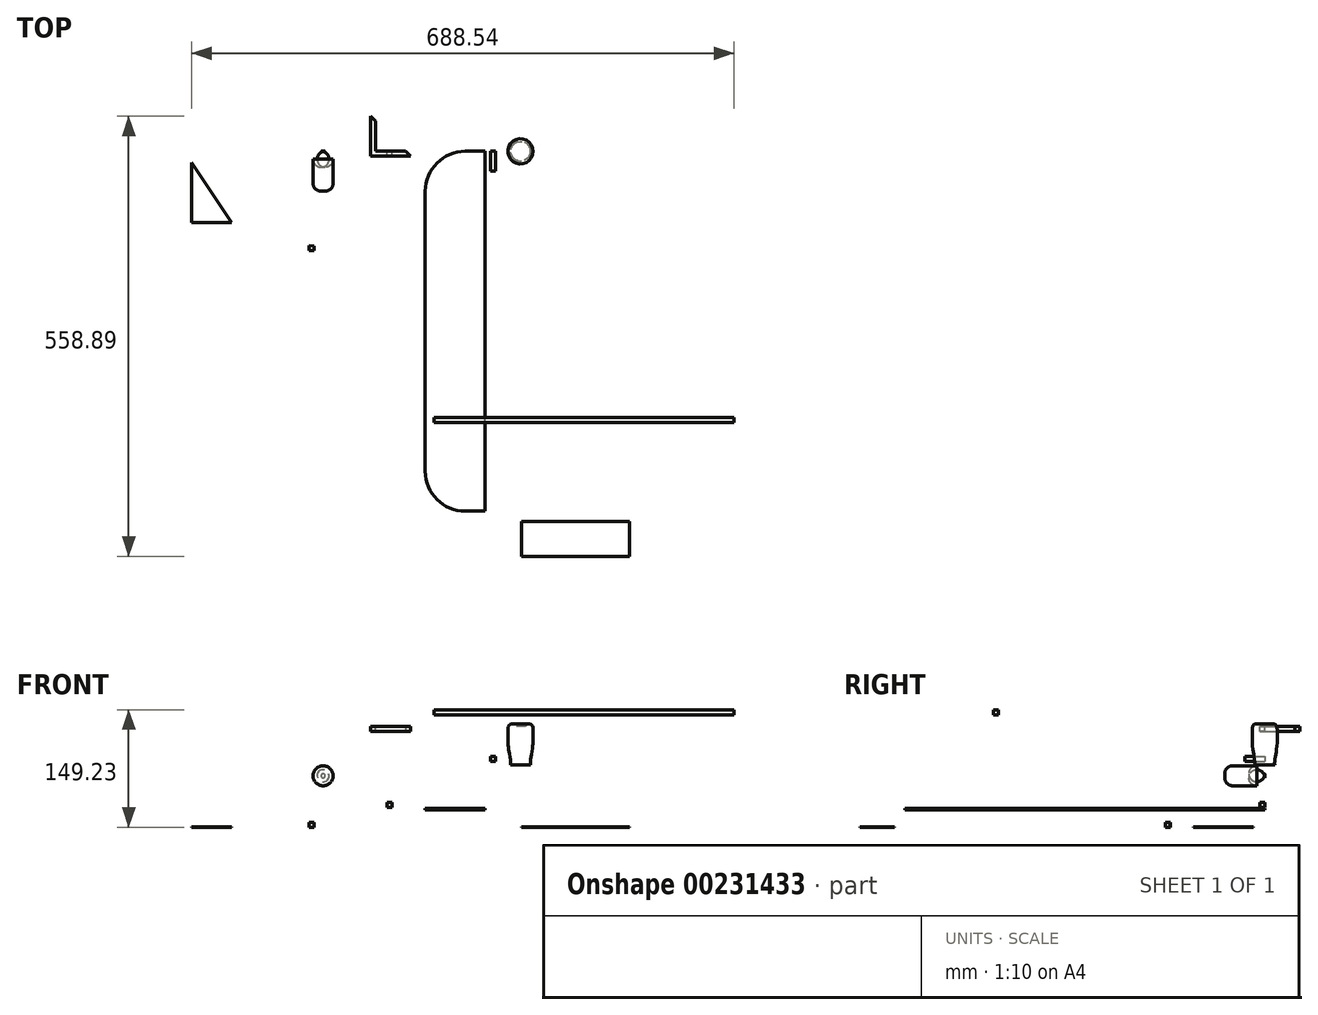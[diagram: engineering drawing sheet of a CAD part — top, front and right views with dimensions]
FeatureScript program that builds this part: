
annotation { "Feature Type Name" : "Feature", "Feature Type Description" : "" }
export const myFeature = defineFeature(function(context is Context, id is Id, definition is map)
    precondition{}
    {
        {
            var Q0;
            Q0=qCreatedBy(makeId("Front.planeOp"),FACE);
            var sketch = newSketch(context, id + "F0", { "sketchPlane" : qUnion([Q0])});
            skLineSegment(sketch, "E0.bottom", {"start": v(-10.86, 23.84) * mm, "end": v(65.34, 23.84) * mm});
            skLineSegment(sketch, "E0.top", {"start": v(-10.86, 22.25) * mm, "end": v(65.34, 22.25) * mm});
            skLineSegment(sketch, "E0.left", {"start": v(-10.86, 23.84) * mm, "end": v(-10.86, 22.25) * mm});
            skLineSegment(sketch, "E0.right", {"start": v(65.34, 23.84) * mm, "end": v(65.34, 22.25) * mm});
            skSolve(sketch);
        }
        {
            var Q0;
            Q0=makeQuery(id+"F0.imprint","IMPRINT",FACE,{"disambiguationData":[TD([[makeQuery(id+"F0.imprint","IMPRINT",EDGE,{"derivedFrom":sQuery(id+"F0.wireOp",EDGE,"E0.bottom")}),-1.0]])]});
            extrude(context, id + "F1", {"entities" : qUnion([Q0]), "depth" : 457.2 * mm});
        }
        {
            var Q0;
            Q0=qCreatedBy(makeId("Right.planeOp"),FACE);
            var sketch = newSketch(context, id + "F2", { "sketchPlane" : qUnion([Q0])});
            skLineSegment(sketch, "E1.bottom", {"start": v(-344.61, 149.23) * mm, "end": v(-338.26, 149.23) * mm});
            skLineSegment(sketch, "E1.top", {"start": v(-344.61, 142.88) * mm, "end": v(-338.26, 142.88) * mm});
            skLineSegment(sketch, "E1.left", {"start": v(-344.61, 149.23) * mm, "end": v(-344.61, 142.88) * mm});
            skLineSegment(sketch, "E1.right", {"start": v(-338.26, 149.23) * mm, "end": v(-338.26, 142.88) * mm});
            skSolve(sketch);
        }
        {
            var Q0;
            Q0=makeQuery(id+"F2.imprint","IMPRINT",FACE,{"disambiguationData":[TD([[makeQuery(id+"F2.imprint","IMPRINT",EDGE,{"derivedFrom":sQuery(id+"F2.wireOp",EDGE,"E1.bottom")}),-1.0]])]});
            extrude(context, id + "F3", {"entities" : qUnion([Q0]), "depth" : 381 * mm});
        }
        {
            var Q0;
            Q0=qCreatedBy(makeId("Front.planeOp"),FACE);
            var sketch = newSketch(context, id + "F4", { "sketchPlane" : qUnion([Q0])});
            skLineSegment(sketch, "E2.bottom", {"start": v(-80.6, 122) * mm, "end": v(-74.24, 122) * mm});
            skLineSegment(sketch, "E2.top", {"start": v(-80.6, 71.2) * mm, "end": v(-74.24, 71.2) * mm});
            skLineSegment(sketch, "E2.left", {"start": v(-80.6, 122) * mm, "end": v(-80.6, 71.2) * mm});
            skLineSegment(sketch, "E2.right", {"start": v(-74.24, 122) * mm, "end": v(-74.24, 71.2) * mm});
            skLineSegment(sketch, "E3.bottom", {"start": v(-74.24, 122) * mm, "end": v(-29.8, 122) * mm});
            skLineSegment(sketch, "E3.top", {"start": v(-74.24, 115.65) * mm, "end": v(-29.8, 115.65) * mm});
            skLineSegment(sketch, "E3.left", {"start": v(-74.24, 122) * mm, "end": v(-74.24, 115.65) * mm});
            skLineSegment(sketch, "E3.right", {"start": v(-29.8, 122) * mm, "end": v(-29.8, 115.65) * mm});
            skSolve(sketch);
        }
        {
            var Q0;
            Q0=makeQuery(id+"F4.imprint","IMPRINT",FACE,{"disambiguationData":[TD([[makeQuery(id+"F4.imprint","IMPRINT",EDGE,{"derivedFrom":sQuery(id+"F4.wireOp",EDGE,"E3.bottom")}),-1.0]])]});
            var Q1;
            Q1=makeQuery(id+"F4.imprint","IMPRINT",FACE,{"disambiguationData":[TD([[makeQuery(id+"F4.imprint","IMPRINT",EDGE,{"derivedFrom":sQuery(id+"F4.wireOp",EDGE,"E2.bottom")}),-1.0]])]});
            extrude(context, id + "F5", {"entities" : qUnion([Q0, Q1]), "depth" : 6.35 * mm});
        }
        {
            var Q0;
            Q0=makeQuery(id+"F5.opExtrude","SWEPT_EDGE",EDGE,{"disambiguationData":[OSD([sQuery(id+"F4.wireOp",EDGE,"E3.top"),sQuery(id+"F4.wireOp",EDGE,"E3.right")])]});
            chamfer(context, id + "F6", {"entities" : qUnion([Q0]), "chamferType" : ChamferType.OFFSET_ANGLE, "width" : 6.35 * mm, "oppositeDirection" : false, "angle" : 45 * degree, "tangentPropagation" : true});
        }
        {
            var Q0;
            Q0=makeQuery(id+"F5.opExtrude","SWEPT_EDGE",EDGE,{"disambiguationData":[OSD([sQuery(id+"F4.wireOp",EDGE,"E2.top"),sQuery(id+"F4.wireOp",EDGE,"E2.right")])]});
            chamfer(context, id + "F7", {"entities" : qUnion([Q0]), "chamferType" : ChamferType.OFFSET_ANGLE, "width" : 6.35 * mm, "oppositeDirection" : false, "angle" : 45 * degree, "tangentPropagation" : true});
        }
        {
            var Q0;
            Q0=makeQuery(id+"F5.opExtrude","SWEPT_BODY",BODY,{"disambiguationData":[OSD([sQuery(id+"F4.wireOp",EDGE,"E2.bottom"),sQuery(id+"F4.wireOp",EDGE,"E2.top"),sQuery(id+"F4.wireOp",EDGE,"E2.left"),sQuery(id+"F4.wireOp",EDGE,"E2.right"),sQuery(id+"F4.wireOp",EDGE,"E3.bottom"),sQuery(id+"F4.wireOp",EDGE,"E3.top"),sQuery(id+"F4.wireOp",EDGE,"E3.right")])]});
            var Q1;
            Q1=makeQuery(id+"F5.opExtrude","CAP_EDGE",EDGE,{"disambiguationData":[OSD([sQuery(id+"F4.wireOp",EDGE,"E2.bottom"),sQuery(id+"F4.wireOp",EDGE,"E3.bottom")])],"isStart":false});
            transform(context, id + "F8", {"entities" : qUnion([Q0]), "transformType" : TransformType.ROTATION, "transformAxis" : qUnion([Q1]), "angle" : 90 * degree, "makeCopy" : false});
        }
        {
            var Q0;
            Q0=qCreatedBy(makeId("Front.planeOp"),FACE);
            var sketch = newSketch(context, id + "F9", { "sketchPlane" : qUnion([Q0])});
            skLineSegment(sketch, "E4.bottom", {"start": v(-59.33, 31.83) * mm, "end": v(-52.98, 31.83) * mm});
            skLineSegment(sketch, "E4.top", {"start": v(-59.33, 25.48) * mm, "end": v(-52.98, 25.48) * mm});
            skLineSegment(sketch, "E4.left", {"start": v(-59.33, 31.83) * mm, "end": v(-59.33, 25.48) * mm});
            skLineSegment(sketch, "E4.right", {"start": v(-52.98, 31.83) * mm, "end": v(-52.98, 25.48) * mm});
            skSolve(sketch);
        }
        {
            var Q0;
            Q0=makeQuery(id+"F9.imprint","IMPRINT",FACE,{"disambiguationData":[TD([[makeQuery(id+"F9.imprint","IMPRINT",EDGE,{"derivedFrom":sQuery(id+"F9.wireOp",EDGE,"E4.bottom")}),-1.0]])]});
            extrude(context, id + "F10", {"entities" : qUnion([Q0]), "depth" : 6.35 * mm});
        }
        {
            var Q0;
            Q0=makeQuery(id+"F1.opExtrude","CAP_EDGE",EDGE,{"disambiguationData":[OSD([sQuery(id+"F0.wireOp",EDGE,"E0.left")])],"isStart":false});
            fillet(context, id + "F11", {"entities" : qUnion([Q0]), "radius" : 50.8 * mm, "tangentPropagation" : true, "allowEdgeOverflow" : false});
        }
        {
            var Q0;
            Q0=makeQuery(id+"F1.opExtrude","CAP_EDGE",EDGE,{"disambiguationData":[OSD([sQuery(id+"F0.wireOp",EDGE,"E0.left")])],"isStart":true});
            fillet(context, id + "F12", {"entities" : qUnion([Q0]), "radius" : 50.8 * mm, "tangentPropagation" : true, "allowEdgeOverflow" : false});
        }
        {
            var Q0;
            Q0=qCreatedBy(makeId("Top.planeOp"),FACE);
            var sketch = newSketch(context, id + "F13", { "sketchPlane" : qUnion([Q0])});
            skLineSegment(sketch, "E5.bottom", {"start": v(111.12, -514.44) * mm, "end": v(248.28, -514.44) * mm});
            skLineSegment(sketch, "E5.top", {"start": v(111.12, -470.44) * mm, "end": v(248.28, -470.44) * mm});
            skLineSegment(sketch, "E5.left", {"start": v(111.12, -514.44) * mm, "end": v(111.12, -470.44) * mm});
            skLineSegment(sketch, "E5.right", {"start": v(248.28, -514.44) * mm, "end": v(248.28, -470.44) * mm});
            skSolve(sketch);
        }
        {
            var Q0;
            Q0=makeQuery(id+"F13.imprint","IMPRINT",FACE,{"disambiguationData":[TD([[makeQuery(id+"F13.imprint","IMPRINT",EDGE,{"derivedFrom":sQuery(id+"F13.wireOp",EDGE,"E5.bottom")}),1.0]])]});
            extrude(context, id + "F14", {"entities" : qUnion([Q0]), "depth" : 0.6 * mm});
        }
        {
            var Q0;
            Q0=qCreatedBy(makeId("Front.planeOp"),FACE);
            var sketch = newSketch(context, id + "F15", { "sketchPlane" : qUnion([Q0])});
            skLineSegment(sketch, "E6.bottom", {"start": v(72.23, 90.15) * mm, "end": v(78.58, 90.15) * mm});
            skLineSegment(sketch, "E6.top", {"start": v(72.23, 83.8) * mm, "end": v(78.58, 83.8) * mm});
            skLineSegment(sketch, "E6.left", {"start": v(72.23, 90.15) * mm, "end": v(72.23, 83.8) * mm});
            skLineSegment(sketch, "E6.right", {"start": v(78.58, 90.15) * mm, "end": v(78.58, 83.8) * mm});
            skSolve(sketch);
        }
        {
            var Q0;
            Q0=makeQuery(id+"F15.imprint","IMPRINT",FACE,{"disambiguationData":[TD([[makeQuery(id+"F15.imprint","IMPRINT",EDGE,{"derivedFrom":sQuery(id+"F15.wireOp",EDGE,"E6.bottom")}),-1.0]])]});
            extrude(context, id + "F16", {"entities" : qUnion([Q0]), "depth" : 25.4 * mm});
        }
        {
            var Q0;
            Q0=qCreatedBy(makeId("Top.planeOp"),FACE);
            var sketch = newSketch(context, id + "F17", { "sketchPlane" : qUnion([Q0])});
            skLineSegment(sketch, "E7", {"start": v(-307.54, -90.8) * mm, "end": v(-256.74, -90.8) * mm});
            skLineSegment(sketch, "E8", {"start": v(-256.74, -90.8) * mm, "end": v(-307.54, -14.6) * mm});
            skLineSegment(sketch, "E9", {"start": v(-307.54, -14.6) * mm, "end": v(-307.54, -90.8) * mm});
            skSolve(sketch);
        }
        {
            var Q0;
            Q0=makeQuery(id+"F17.imprint","IMPRINT",FACE,{"disambiguationData":[TD([[makeQuery(id+"F17.imprint","IMPRINT",EDGE,{"derivedFrom":sQuery(id+"F17.wireOp",EDGE,"E7")}),1.0]])]});
            extrude(context, id + "F18", {"entities" : qUnion([Q0]), "depth" : 0.6 * mm});
        }
        {
            var Q0;
            Q0=qCreatedBy(makeId("Top.planeOp"),FACE);
            var sketch = newSketch(context, id + "F19", { "sketchPlane" : qUnion([Q0])});
            skLineSegment(sketch, "E10", {"start": v(-158.2, -126.22) * mm, "end": v(-151.86, -126.22) * mm});
            skLineSegment(sketch, "E11", {"start": v(-151.86, -126.22) * mm, "end": v(-151.86, -120.42) * mm});
            skLineSegment(sketch, "E12", {"start": v(-151.86, -120.42) * mm, "end": v(-158.2, -119.87) * mm});
            skLineSegment(sketch, "E13", {"start": v(-158.2, -119.87) * mm, "end": v(-158.2, -126.22) * mm});
            skSolve(sketch);
        }
        {
            var Q0;
            Q0=makeQuery(id+"F19.imprint","IMPRINT",FACE,{"disambiguationData":[TD([[makeQuery(id+"F19.imprint","IMPRINT",EDGE,{"derivedFrom":sQuery(id+"F19.wireOp",EDGE,"E10")}),1.0]])]});
            extrude(context, id + "F20", {"entities" : qUnion([Q0]), "depth" : 6.35 * mm});
        }
        {
            var Q0;
            Q0=qCreatedBy(makeId("Front.planeOp"),FACE);
            var sketch = newSketch(context, id + "F21", { "sketchPlane" : qUnion([Q0])});
            skCircle(sketch, "E14", {"center": v(-140.67, 65.36) * mm, "radius": 12.7 * mm});
            skSolve(sketch);
        }
        {
            var Q0;
            Q0=makeQuery(id+"F21.imprint","IMPRINT",FACE,{"disambiguationData":[TD([[makeQuery(id+"F21.imprint","IMPRINT",EDGE,{"derivedFrom":sQuery(id+"F21.wireOp",EDGE,"E14")}),1.0]])]});
            extrude(context, id + "F22", {"entities" : qUnion([Q0]), "depth" : 50.8 * mm});
        }
        {
            var Q0;
            Q0=makeQuery(id+"F22.opExtrude","CAP_EDGE",EDGE,{"disambiguationData":[OSD([sQuery(id+"F21.wireOp",EDGE,"E14")])],"isStart":false});
            fillet(context, id + "F23", {"entities" : qUnion([Q0]), "radius" : 10.16 * mm, "tangentPropagation" : true, "allowEdgeOverflow" : false});
        }
        {
            var Q0;
            Q0=makeQuery(id+"F22.opExtrude","CAP_EDGE",EDGE,{"disambiguationData":[OSD([sQuery(id+"F21.wireOp",EDGE,"E14")])],"isStart":true});
            fillet(context, id + "F24", {"entities" : qUnion([Q0]), "radius" : 10.16 * mm, "tangentPropagation" : true, "allowEdgeOverflow" : false});
        }
        {
            var Q0;
            Q0=qCreatedBy(makeId("Front.planeOp"),FACE);
            var sketch = newSketch(context, id + "F25", { "sketchPlane" : qUnion([Q0])});
            skLineSegment(sketch, "E15", {"start": v(110.08, 130.08) * mm, "end": v(110.08, 79.28) * mm});
            skLineSegment(sketch, "E16", {"start": v(110.08, 79.28) * mm, "end": v(122.78, 79.28) * mm});
            skFitSpline(sketch, "E17", {"points": [v(110.08, 130.08) * mm, v(111.54, 130.08) * mm, v(115, 128.59) * mm, v(118.4, 130.08) * mm, v(123.16, 130.8) * mm, v(125.78, 126.46) * mm, v(125.93, 115.88) * mm, v(125.62, 103) * mm, v(122.6, 81.76) * mm, v(122.78, 79.28) * mm], "startDerivative": vector(16.24, 1.6) * mm, "endDerivative": vector(3.2, -22.57) * mm});
            skSolve(sketch);
        }
        {
            var Q0;
            Q0=makeQuery(id+"F25.imprint","IMPRINT",FACE,{"disambiguationData":[TD([[makeQuery(id+"F25.imprint","IMPRINT",EDGE,{"derivedFrom":sQuery(id+"F25.wireOp",EDGE,"E15")}),1.0]])]});
            var Q1;
            Q1=sQuery(id+"F25.wireOp",EDGE,"E15");
            revolve(context, id + "F26", {"entities" : qUnion([Q0]), "axis" : qUnion([Q1]), "revolveType" : RevolveType.FULL});
        }
    });
